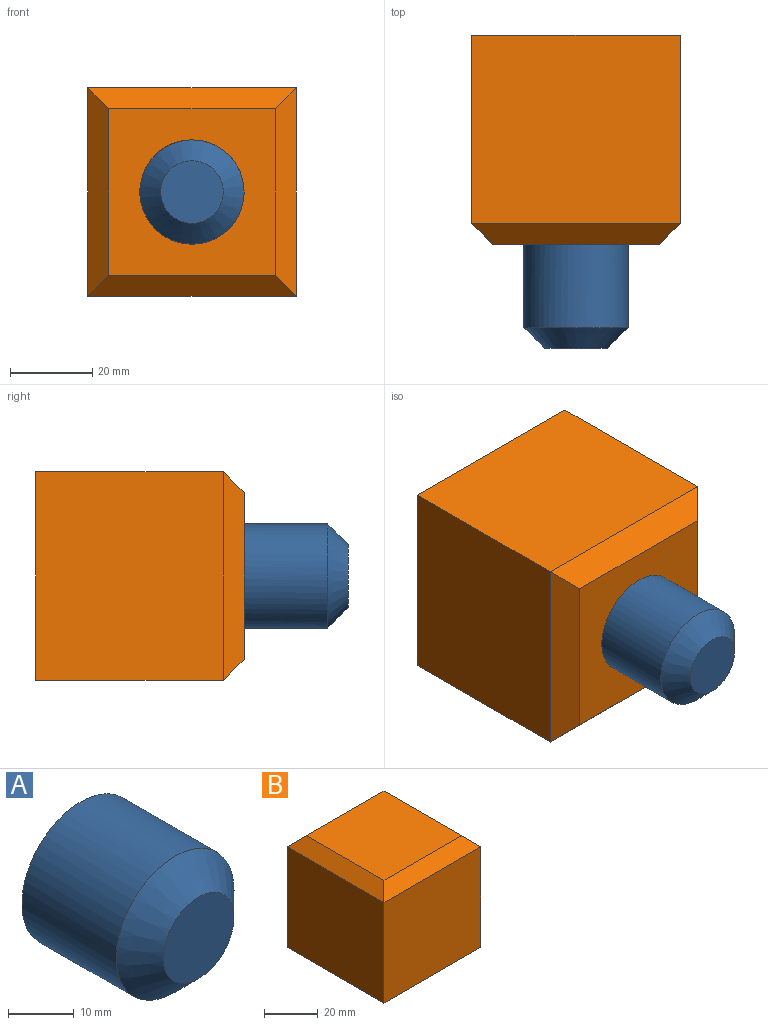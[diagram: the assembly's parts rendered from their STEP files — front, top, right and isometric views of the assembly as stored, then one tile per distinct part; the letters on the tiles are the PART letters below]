
ASSEMBLY  parts=2 mates=2
PART A: 4 faces, bbox 25.4x25.4x25.4 mm
  f0: cylinder r=12.7mm len=25.4mm, axis (0,1,0), area 1621.5mm2, adj f2,f3
  f1: plane 15.24x15.24mm, normal (0,-1,0), area 182.4mm2, adj f3
  f2: plane 25.4x25.4mm, normal (0,1,0), area 506.7mm2, adj f0
  f3: cone r=7.62mm half-angle=45deg, axis (0,1,0), area 458.6mm2, adj f0,f1
PART B: 10 faces, bbox 50.8x50.8x50.8 mm
  f0: plane 50.8x50.8mm, normal (0,0,-1), area 2580.6mm2, adj f1,f3,f4,f5
  f1: plane 50.8x45.72mm, normal (1,0,0), area 2322.6mm2, adj f0,f4,f5,f7
  f2: plane 40.64x40.64mm, normal (0,0,1), area 1651.6mm2, adj f6,f7,f8,f9
  f3: plane 50.8x45.72mm, normal (-1,0,0), area 2322.6mm2, adj f0,f4,f5,f8
  f4: plane 50.8x45.72mm, normal (0,-1,0), area 2322.6mm2, adj f0,f1,f3,f9
  f5: plane 50.8x45.72mm, normal (0,1,0), area 2322.6mm2, adj f0,f1,f3,f6
  f6: plane 50.8x5.08mm, normal (0,0.71,0.71), area 328.5mm2, adj f2,f5,f7,f8
  f7: plane 50.8x5.08mm, normal (0.71,0,0.71), area 328.5mm2, adj f1,f2,f6,f9
  f8: plane 50.8x5.08mm, normal (-0.71,0,0.71), area 328.5mm2, adj f2,f3,f6,f9
  f9: plane 50.8x5.08mm, normal (0,-0.71,0.71), area 328.5mm2, adj f2,f4,f7,f8
PLACE A t=(-40.99,-11.01,17.22)mm
PLACE B rot(axis=(1,0,0),90deg) t=(-40.27,14.39,42.62)mm
MATE planar B.f2 <-> A.f0  axis (0,-1,0) through (-40.99,-11.01,17.22)mm
MATE fastened B.f2 <-> A.f0  axis (0,-1,0) through (-40.99,-11.01,17.22)mm
